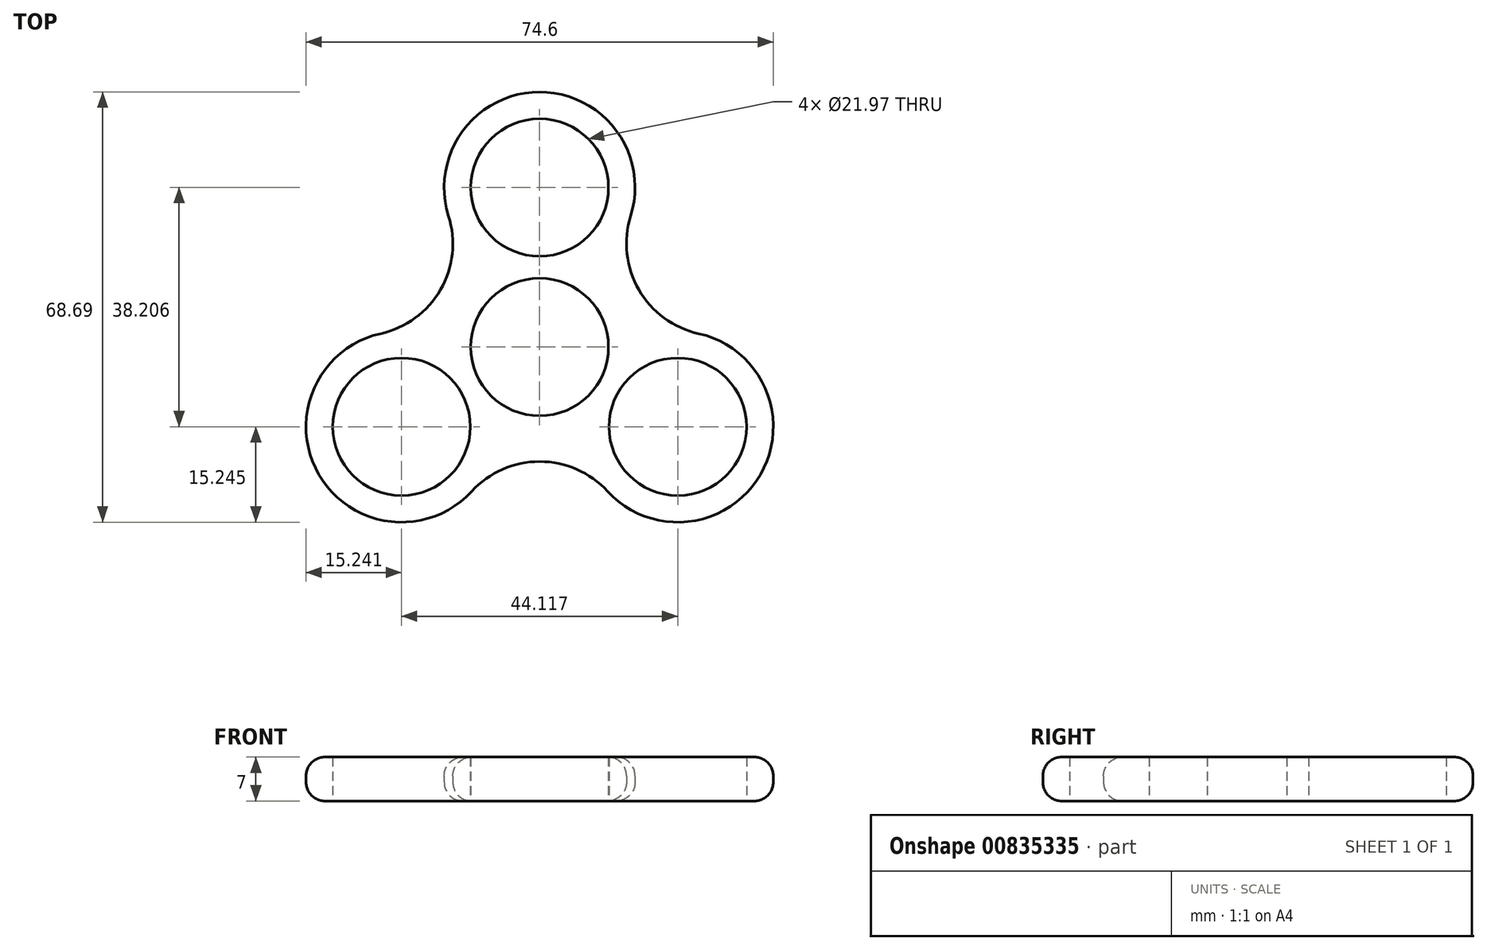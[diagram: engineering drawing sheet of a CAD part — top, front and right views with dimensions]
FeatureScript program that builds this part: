
annotation { "Feature Type Name" : "Feature", "Feature Type Description" : "" }
export const myFeature = defineFeature(function(context is Context, id is Id, definition is map)
    precondition{}
    {
        {
            var Q0;
            Q0=qCreatedBy(makeId("Top.planeOp"),FACE);
            var sketch = newSketch(context, id + "F0", { "sketchPlane" : qUnion([Q0])});
            skCircle(sketch, "E0", {"center": v(0, 0) * mm, "radius": 10.99 * mm});
            skCircle(sketch, "E1", {"center": v(0, 0) * mm, "radius": 25.47 * mm, "construction": true});
            skCircle(sketch, "E2", {"center": v(0, 25.47) * mm, "radius": 10.99 * mm});
            skCircle(sketch, "E3", {"center": v(-22.06, -12.74) * mm, "radius": 10.99 * mm});
            skCircle(sketch, "E4", {"center": v(22.06, -12.74) * mm, "radius": 10.99 * mm});
            skLineSegment(sketch, "E5", {"start": v(-22.06, -12.74) * mm, "end": v(22.06, -12.74) * mm, "construction": true});
            skLineSegment(sketch, "E6", {"start": v(0, 25.47) * mm, "end": v(-22.06, -12.74) * mm, "construction": true});
            skLineSegment(sketch, "E7", {"start": v(22.06, -12.74) * mm, "end": v(0, 25.47) * mm, "construction": true});
            skLineSegment(sketch, "E8.bottom", {"start": v(-57.15, 57.15) * mm, "end": v(57.15, 57.15) * mm, "construction": true});
            skLineSegment(sketch, "E8.top", {"start": v(-57.15, -57.15) * mm, "end": v(57.15, -57.15) * mm, "construction": true});
            skLineSegment(sketch, "E8.left", {"start": v(-57.15, 57.15) * mm, "end": v(-57.15, -57.15) * mm, "construction": true});
            skLineSegment(sketch, "E8.right", {"start": v(57.15, 57.15) * mm, "end": v(57.15, -57.15) * mm, "construction": true});
            skPoint(sketch, "E9", {"position": v(-57.15, 0) * mm});
            skPoint(sketch, "E10", {"position": v(0, 57.15) * mm});
            skArc(sketch, "E11", {"start": v(14.54, 20.91) * mm, "mid": v(0, 40.71) * mm, "end": v(-14.54, 20.91) * mm});
            skArc(sketch, "E12", {"start": v(10.84, -23.05) * mm, "mid": v(35.26, -20.36) * mm, "end": v(25.38, 2.14) * mm});
            skArc(sketch, "E13", {"start": v(-25.38, 2.14) * mm, "mid": v(-35.26, -20.36) * mm, "end": v(-10.84, -23.05) * mm});
            skArc(sketch, "E14", {"start": v(10.84, -23.05) * mm, "mid": v(0, -18.3) * mm, "end": v(-10.84, -23.05) * mm});
            skArc(sketch, "E15", {"start": v(-25.38, 2.14) * mm, "mid": v(-15.84, 9.15) * mm, "end": v(-14.54, 20.91) * mm});
            skArc(sketch, "E16", {"start": v(14.54, 20.91) * mm, "mid": v(15.84, 9.15) * mm, "end": v(25.38, 2.14) * mm});
            skSolve(sketch);
        }
        {
            var Q0;
            Q0 = qSketchRegion(id + "F0", true);
            extrude(context, id + "F1", {"entities" : qUnion([Q0]), "depth" : 7 * mm, "offsetDistance" : 25.4 * mm});
        }
        {
            var Q0;
            Q0=makeQuery(id+"F1.opExtrude","SWEPT_FACE",FACE,{"disambiguationData":[OSD([sQuery(id+"F0.wireOp",EDGE,"E16")])]});
            fillet(context, id + "F2", {"entities" : qUnion([Q0]), "radius" : 3 * mm, "tangentPropagation" : true, "allowEdgeOverflow" : false});
        }
    });
